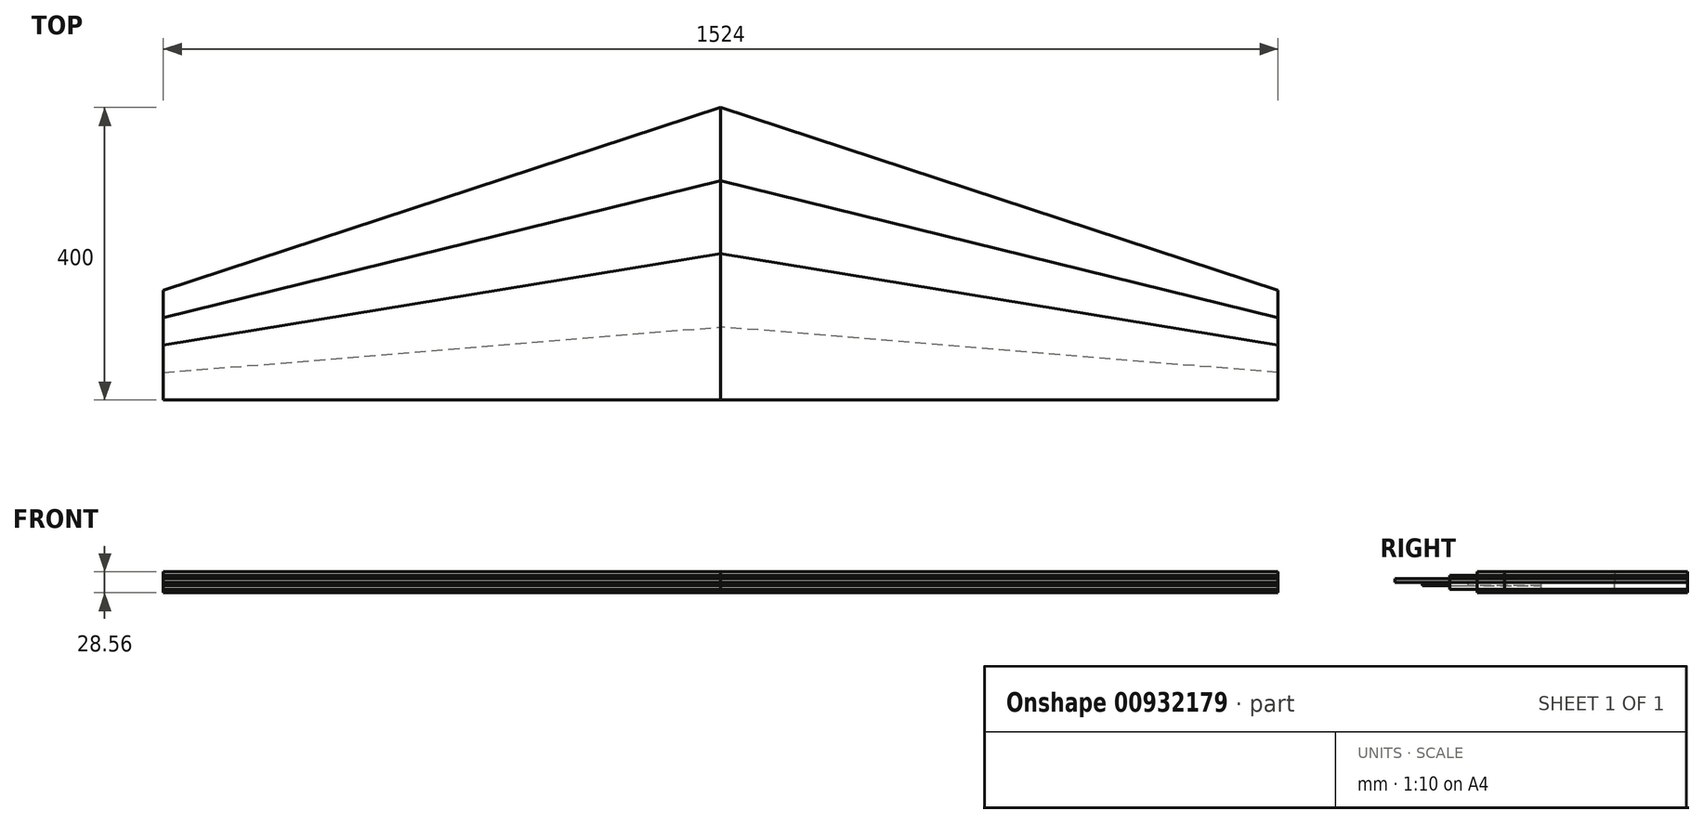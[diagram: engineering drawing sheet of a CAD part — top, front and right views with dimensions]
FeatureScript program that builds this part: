
annotation { "Feature Type Name" : "Feature", "Feature Type Description" : "" }
export const myFeature = defineFeature(function(context is Context, id is Id, definition is map)
    precondition{}
    {
        {
            var Q0;
            Q0=qCreatedBy(makeId("Top.planeOp"),FACE);
            var sketch = newSketch(context, id + "F0", { "sketchPlane" : qUnion([Q0])});
            skLineSegment(sketch, "E0.bottom", {"start": v(381, 254) * mm, "end": v(-381, 254) * mm, "construction": true});
            skPoint(sketch, "E0.middle", {"position": v(0, 0) * mm});
            skLineSegment(sketch, "E1", {"start": v(-381, -104) * mm, "end": v(381, 146) * mm});
            skLineSegment(sketch, "E2", {"start": v(-381, -179) * mm, "end": v(381, -54) * mm});
            skLineSegment(sketch, "E3", {"start": v(-381, -141.5) * mm, "end": v(381, 46) * mm});
            skLineSegment(sketch, "E4", {"start": v(381, 146) * mm, "end": v(-381, 146) * mm, "construction": true});
            skLineSegment(sketch, "E5", {"start": v(381, 46) * mm, "end": v(-381, 46) * mm, "construction": true});
            skLineSegment(sketch, "E6", {"start": v(381, -54) * mm, "end": v(-381, -54) * mm, "construction": true});
            skLineSegment(sketch, "E7", {"start": v(381, -254) * mm, "end": v(-381, -254) * mm});
            skLineSegment(sketch, "E8", {"start": v(-381, -254) * mm, "end": v(-381, -179) * mm});
            skLineSegment(sketch, "E9", {"start": v(-381, -179) * mm, "end": v(-381, -141.5) * mm});
            skLineSegment(sketch, "E10", {"start": v(-381, -104) * mm, "end": v(-381, -141.5) * mm});
            skLineSegment(sketch, "E11", {"start": v(381, 146) * mm, "end": v(381, 46) * mm});
            skLineSegment(sketch, "E12", {"start": v(381, -54) * mm, "end": v(381, 46) * mm});
            skLineSegment(sketch, "E13", {"start": v(381, -54) * mm, "end": v(381, -254) * mm});
            skLineSegment(sketch, "E14", {"start": v(-381, -216.5) * mm, "end": v(381, -154) * mm});
            skSolve(sketch);
        }
        {
            var Q0;
            Q0=makeQuery(id+"F0.imprint","IMPRINT",FACE,{"disambiguationData":[TD([[makeQuery(id+"F0.imprint","IMPRINT",EDGE,{"derivedFrom":sQuery(id+"F0.wireOp",EDGE,"E2")}),-1.0]])]});
            var Q1;
            Q1=makeQuery(id+"F0.imprint","IMPRINT",FACE,{"disambiguationData":[TD([[makeQuery(id+"F0.imprint","IMPRINT",EDGE,{"derivedFrom":sQuery(id+"F0.wireOp",EDGE,"E2")}),1.0]])]});
            var Q2;
            Q2=makeQuery(id+"F0.imprint","IMPRINT",FACE,{"disambiguationData":[TD([[makeQuery(id+"F0.imprint","IMPRINT",EDGE,{"derivedFrom":sQuery(id+"F0.wireOp",EDGE,"E1")}),-1.0]])]});
            var Q3;
            {var subQ0=sQuery(id+"F0.wireOp",EDGE,"E7");Q3=makeQuery(id+"F0.imprint","IMPRINT",FACE,{"disambiguationData":[TD([[makeQuery(id+"F0.imprint","IMPRINT",EDGE,{"derivedFrom":subQ0}),-1.0]])]});}
            extrude(context, id + "F1", {"entities" : qUnion([Q0, Q1, Q2, Q3]), "depth" : 4.76 * mm, "offsetDistance" : 25 * mm});
        }
        {
            var Q0;
            Q0=makeQuery(id+"F0.imprint","IMPRINT",FACE,{"disambiguationData":[TD([[makeQuery(id+"F0.imprint","IMPRINT",EDGE,{"derivedFrom":sQuery(id+"F0.wireOp",EDGE,"E2")}),1.0]])]});
            var Q1;
            Q1=makeQuery(id+"F0.imprint","IMPRINT",FACE,{"disambiguationData":[TD([[makeQuery(id+"F0.imprint","IMPRINT",EDGE,{"derivedFrom":sQuery(id+"F0.wireOp",EDGE,"E1")}),-1.0]])]});
            extrude(context, id + "F2", {"entities" : qUnion([Q0, Q1]), "depth" : (4.76 * 2) * mm, "offsetDistance" : 25 * mm});
        }
        {
            var Q0;
            Q0=makeQuery(id+"F0.imprint","IMPRINT",FACE,{"disambiguationData":[TD([[makeQuery(id+"F0.imprint","IMPRINT",EDGE,{"derivedFrom":sQuery(id+"F0.wireOp",EDGE,"E1")}),-1.0]])]});
            extrude(context, id + "F3", {"entities" : qUnion([Q0]), "depth" : (4.76 * 3) * mm, "offsetDistance" : 25 * mm});
        }
        {
            var Q0;
            Q0=makeQuery(id+"F0.imprint","IMPRINT",FACE,{"disambiguationData":[TD([[makeQuery(id+"F0.imprint","IMPRINT",EDGE,{"derivedFrom":sQuery(id+"F0.wireOp",EDGE,"E2")}),1.0]])]});
            var Q1;
            Q1=makeQuery(id+"F0.imprint","IMPRINT",FACE,{"disambiguationData":[TD([[makeQuery(id+"F0.imprint","IMPRINT",EDGE,{"derivedFrom":sQuery(id+"F0.wireOp",EDGE,"E1")}),-1.0]])]});
            extrude(context, id + "F4", {"entities" : qUnion([Q0, Q1]), "oppositeDirection" : true, "depth" : (4.76 * 2) * mm, "offsetDistance" : 25 * mm});
        }
        {
            var Q0;
            Q0=makeQuery(id+"F0.imprint","IMPRINT",FACE,{"disambiguationData":[TD([[makeQuery(id+"F0.imprint","IMPRINT",EDGE,{"derivedFrom":sQuery(id+"F0.wireOp",EDGE,"E1")}),-1.0]])]});
            extrude(context, id + "F5", {"entities" : qUnion([Q0]), "oppositeDirection" : true, "depth" : (4.76 * 3) * mm, "offsetDistance" : 25 * mm});
        }
        {
            var Q0;
            {var subQ0=sQuery(id+"F0.wireOp",EDGE,"E2");Q0=makeQuery(id+"F0.imprint","IMPRINT",FACE,{"disambiguationData":[TD([[makeQuery(id+"F0.imprint","IMPRINT",EDGE,{"derivedFrom":subQ0}),-1.0]])]});}
            extrude(context, id + "F6", {"entities" : qUnion([Q0]), "oppositeDirection" : true, "depth" : 4.78 * mm, "offsetDistance" : 25 * mm});
        }
        {
            var Q0;
            Q0=makeQuery(id+"F1.opExtrude","SWEPT_BODY",BODY,{"disambiguationData":[OSD([sQuery(id+"F0.wireOp",EDGE,"E1"),sQuery(id+"F0.wireOp",EDGE,"E7"),sQuery(id+"F0.wireOp",EDGE,"E8"),sQuery(id+"F0.wireOp",EDGE,"E9"),sQuery(id+"F0.wireOp",EDGE,"E10"),sQuery(id+"F0.wireOp",EDGE,"E11"),sQuery(id+"F0.wireOp",EDGE,"E12"),sQuery(id+"F0.wireOp",EDGE,"E13")])]});
            var Q1;
            Q1=makeQuery(id+"F2.opExtrude","SWEPT_BODY",BODY,{"disambiguationData":[OSD([sQuery(id+"F0.wireOp",EDGE,"E1"),sQuery(id+"F0.wireOp",EDGE,"E2"),sQuery(id+"F0.wireOp",EDGE,"E9"),sQuery(id+"F0.wireOp",EDGE,"E10"),sQuery(id+"F0.wireOp",EDGE,"E11"),sQuery(id+"F0.wireOp",EDGE,"E12")])]});
            var Q2;
            Q2=makeQuery(id+"F3.opExtrude","SWEPT_BODY",BODY,{"disambiguationData":[OSD([sQuery(id+"F0.wireOp",EDGE,"E1"),sQuery(id+"F0.wireOp",EDGE,"E3"),sQuery(id+"F0.wireOp",EDGE,"E10"),sQuery(id+"F0.wireOp",EDGE,"E11")])]});
            var Q3;
            Q3=makeQuery(id+"F4.opExtrude","SWEPT_BODY",BODY,{"disambiguationData":[OSD([sQuery(id+"F0.wireOp",EDGE,"E1"),sQuery(id+"F0.wireOp",EDGE,"E2"),sQuery(id+"F0.wireOp",EDGE,"E9"),sQuery(id+"F0.wireOp",EDGE,"E10"),sQuery(id+"F0.wireOp",EDGE,"E11"),sQuery(id+"F0.wireOp",EDGE,"E12")])]});
            var Q4;
            Q4=makeQuery(id+"F5.opExtrude","SWEPT_BODY",BODY,{"disambiguationData":[OSD([sQuery(id+"F0.wireOp",EDGE,"E1"),sQuery(id+"F0.wireOp",EDGE,"E3"),sQuery(id+"F0.wireOp",EDGE,"E10"),sQuery(id+"F0.wireOp",EDGE,"E11")])]});
            var Q5;
            Q5=makeQuery(id+"F6.opExtrude","SWEPT_BODY",BODY,{"disambiguationData":[OSD([sQuery(id+"F0.wireOp",EDGE,"E2"),sQuery(id+"F0.wireOp",EDGE,"E8"),sQuery(id+"F0.wireOp",EDGE,"E13"),sQuery(id+"F0.wireOp",EDGE,"E14")])]});
            var Q6;
            {var subQ0=sQuery(id+"F0.wireOp",EDGE,"E13");var subQ1=sQuery(id+"F0.wireOp",EDGE,"E11");var subQ2=sQuery(id+"F0.wireOp",EDGE,"E12");Q6=makeQuery(id+"F6.boolean.opBoolean","MERGE",FACE,{"derivedFrom":[makeQuery(id+"F5.boolean.opBoolean","MERGE",FACE,{"derivedFrom":[makeQuery(id+"F4.boolean.opBoolean","MERGE",FACE,{"derivedFrom":[makeQuery(id+"F3.boolean.opBoolean","MERGE",FACE,{"derivedFrom":[makeQuery(id+"F2.boolean.opBoolean","MERGE",FACE,{"derivedFrom":[makeQuery(id+"F1.opExtrude","SWEPT_FACE",FACE,{"disambiguationData":[OSD([subQ1,subQ2,subQ0])]}),makeQuery(id+"F2.opExtrude","SWEPT_FACE",FACE,{"disambiguationData":[OSD([subQ1,subQ2])]})]}),makeQuery(id+"F3.opExtrude","SWEPT_FACE",FACE,{"disambiguationData":[OSD([subQ1])]})]}),makeQuery(id+"F4.opExtrude","SWEPT_FACE",FACE,{"disambiguationData":[OSD([subQ1,subQ2])]})]}),makeQuery(id+"F5.opExtrude","SWEPT_FACE",FACE,{"disambiguationData":[OSD([subQ1])]})]}),makeQuery(id+"F6.opExtrude","SWEPT_FACE",FACE,{"disambiguationData":[OSD([subQ0])]})]});}
            mirror(context, id + "F7", {"entities" : qUnion([Q0, Q1, Q2, Q3, Q4, Q5]), "mirrorPlane" : qUnion([Q6])});
        }
    });
